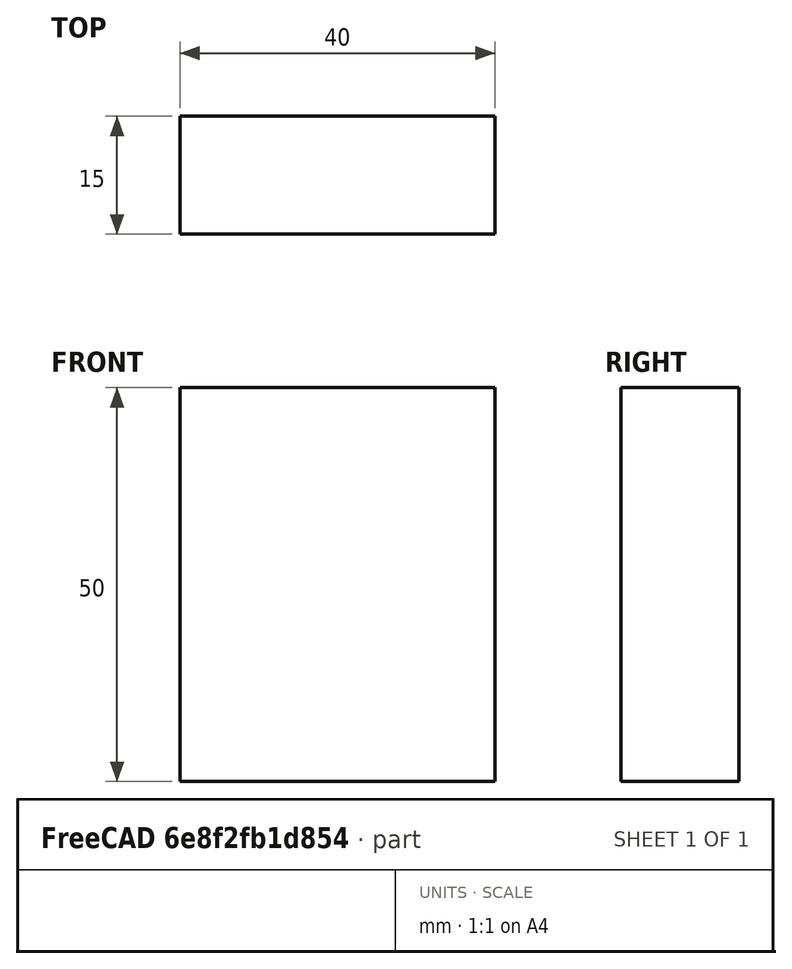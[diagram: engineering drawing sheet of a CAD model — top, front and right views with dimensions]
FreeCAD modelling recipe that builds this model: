
FCSTD DOCUMENT  (FreeCAD 0.15R4671 (Git))
Label: Flat Bar 40x15 EN10058 S235JR
License: All rights reserved
LicenseURL: http://en.wikipedia.org/wiki/All_rights_reserved
objects: Sketcher::SketchObject×1, Part::Extrusion×1
note: 2 computed .brp shape members not serialized (recipe doc carries the construction recipe); baked Part::Feature solids carry a one-line shape summary decoded from their .brp

FEATURE [Sketcher::SketchObject] Sketch
  sketch-geometry (4):
    g0: LineSegment StartX=-20 StartY=-7.5 StartZ=0 EndX=20 EndY=-7.5 EndZ=0
    g1: LineSegment StartX=20 StartY=-7.5 StartZ=0 EndX=20 EndY=7.5 EndZ=0
    g2: LineSegment StartX=20 StartY=7.5 StartZ=0 EndX=-20 EndY=7.5 EndZ=0
    g3: LineSegment StartX=-20 StartY=7.5 StartZ=0 EndX=-20 EndY=-7.5 EndZ=0
  constraints (12):
    c: Coincident(g0,g1)
    c: Coincident(g1,g2)
    c: Coincident(g2,g3)
    c: Coincident(g3,g0)
    c: Horizontal(g0)
    c: Horizontal(g2)
    c: Vertical(g1)
    c: Vertical(g3)
    c: Symmetric(g1,g2,g-2)
    c: Symmetric(g0,g1,g-1)
    c: DistanceY(g1) = 15
    c: DistanceX(g0) = 40
FEATURE [Part::Extrusion] Extrude  label="Flat Bar 40x15 EN10058 S235JR"
  Base = -> Sketch
  Dir = (0,0,50)
  Solid = true
